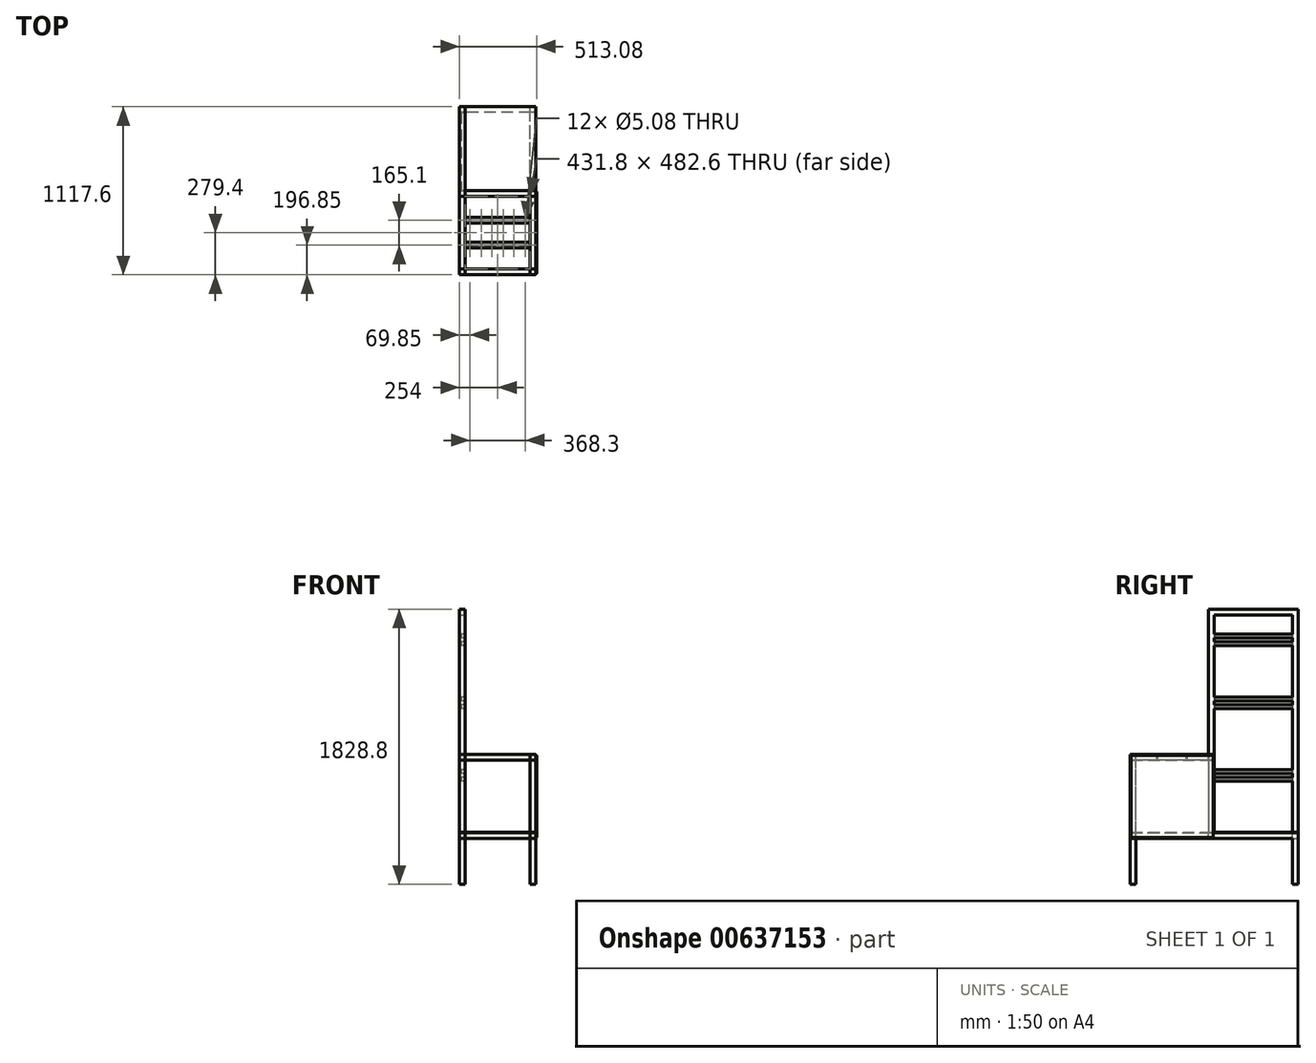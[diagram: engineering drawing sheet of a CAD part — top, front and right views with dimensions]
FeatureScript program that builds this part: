
annotation { "Feature Type Name" : "Feature", "Feature Type Description" : "" }
export const myFeature = defineFeature(function(context is Context, id is Id, definition is map)
    precondition{}
    {
        {
            var Q0;
            Q0=qCreatedBy(makeId("Front.planeOp"),FACE);
            var sketch = newSketch(context, id + "F0", { "sketchPlane" : qUnion([Q0])});
            skLineSegment(sketch, "E0.bottom", {"start": v(-19.05, 19.05) * mm, "end": v(19.05, 19.05) * mm});
            skLineSegment(sketch, "E0.top", {"start": v(-19.05, -19.05) * mm, "end": v(19.05, -19.05) * mm});
            skLineSegment(sketch, "E0.left", {"start": v(-19.05, 19.05) * mm, "end": v(-19.05, -19.05) * mm});
            skLineSegment(sketch, "E0.right", {"start": v(19.05, 19.05) * mm, "end": v(19.05, -19.05) * mm});
            skLineSegment(sketch, "E1", {"start": v(-19.05, 19.05) * mm, "end": v(19.05, -19.05) * mm, "construction": true});
            skLineSegment(sketch, "E2.bottom", {"start": v(450.85, -19.05) * mm, "end": v(488.95, -19.05) * mm});
            skLineSegment(sketch, "E2.top", {"start": v(450.85, 19.05) * mm, "end": v(488.95, 19.05) * mm});
            skLineSegment(sketch, "E2.left", {"start": v(450.85, -19.05) * mm, "end": v(450.85, 19.05) * mm});
            skLineSegment(sketch, "E2.right", {"start": v(488.95, -19.05) * mm, "end": v(488.95, 19.05) * mm});
            skSolve(sketch);
        }
        {
            var Q0;
            Q0 = qSketchRegion(id + "F0", true);
            extrude(context, id + "F1", {"entities" : qUnion([Q0]), "depth" : 1117.6 * mm, "offsetDistance" : 25.4 * mm});
        }
        {
            var Q0;
            Q0=makeQuery(id+"F1.opExtrude","SWEPT_FACE",FACE,{"disambiguationData":[OSD([sQuery(id+"F0.wireOp",EDGE,"E2.bottom")])]});
            var sketch = newSketch(context, id + "F2", { "sketchPlane" : qUnion([Q0])});
            skLineSegment(sketch, "E3.bottom", {"start": v(488.95, 1117.6) * mm, "end": v(450.85, 1117.6) * mm});
            skLineSegment(sketch, "E3.top", {"start": v(488.95, 1079.5) * mm, "end": v(450.85, 1079.5) * mm});
            skLineSegment(sketch, "E3.left", {"start": v(488.95, 1117.6) * mm, "end": v(488.95, 1079.5) * mm});
            skLineSegment(sketch, "E3.right", {"start": v(450.85, 1117.6) * mm, "end": v(450.85, 1079.5) * mm});
            skLineSegment(sketch, "E4.bottom", {"start": v(19.05, 1117.6) * mm, "end": v(-19.05, 1117.6) * mm});
            skLineSegment(sketch, "E4.top", {"start": v(19.05, 1079.5) * mm, "end": v(-19.05, 1079.5) * mm});
            skLineSegment(sketch, "E4.left", {"start": v(19.05, 1117.6) * mm, "end": v(19.05, 1079.5) * mm});
            skLineSegment(sketch, "E4.right", {"start": v(-19.05, 1117.6) * mm, "end": v(-19.05, 1079.5) * mm});
            skSolve(sketch);
        }
        {
            var Q0;
            Q0 = qSketchRegion(id + "F2", true);
            extrude(context, id + "F3", {"entities" : qUnion([Q0]), "depth" : 304.8 * mm, "offsetDistance" : 25.4 * mm, "hasSecondDirection" : true, "secondDirectionOppositeDirection" : true, "secondDirectionDepth" : 558.8 * mm});
        }
        {
            var Q0;
            Q0=makeQuery(id+"F1.opExtrude","SWEPT_FACE",FACE,{"disambiguationData":[OSD([sQuery(id+"F0.wireOp",EDGE,"E0.top")])]});
            var sketch = newSketch(context, id + "F4", { "sketchPlane" : qUnion([Q0])});
            skLineSegment(sketch, "E5.bottom", {"start": v(19.05, 0) * mm, "end": v(-19.05, 0) * mm});
            skLineSegment(sketch, "E5.top", {"start": v(19.05, 38.1) * mm, "end": v(-19.05, 38.1) * mm});
            skLineSegment(sketch, "E5.left", {"start": v(19.05, 0) * mm, "end": v(19.05, 38.1) * mm});
            skLineSegment(sketch, "E5.right", {"start": v(-19.05, 0) * mm, "end": v(-19.05, 38.1) * mm});
            skSolve(sketch);
        }
        {
            var Q0;
            Q0 = qSketchRegion(id + "F4", true);
            extrude(context, id + "F5", {"entities" : qUnion([Q0]), "operationType" : NewBodyOperationType.ADD, "depth" : 304.8 * mm, "offsetDistance" : 25.4 * mm, "hasSecondDirection" : true, "secondDirectionOppositeDirection" : true, "secondDirectionDepth" : 1524 * mm});
        }
        {
            var Q0;
            Q0=makeQuery(id+"F1.opExtrude","SWEPT_FACE",FACE,{"disambiguationData":[OSD([sQuery(id+"F0.wireOp",EDGE,"E0.bottom")])]});
            var sketch = newSketch(context, id + "F6", { "sketchPlane" : qUnion([Q0])});
            skLineSegment(sketch, "E6.bottom", {"start": v(-19.05, -596.9) * mm, "end": v(19.05, -596.9) * mm});
            skLineSegment(sketch, "E6.top", {"start": v(-19.05, -558.8) * mm, "end": v(19.05, -558.8) * mm});
            skLineSegment(sketch, "E6.left", {"start": v(-19.05, -596.9) * mm, "end": v(-19.05, -558.8) * mm});
            skLineSegment(sketch, "E6.right", {"start": v(19.05, -596.9) * mm, "end": v(19.05, -558.8) * mm});
            skSolve(sketch);
        }
        {
            var Q0;
            Q0 = qSketchRegion(id + "F6", true);
            var Q1;
            Q1=makeQuery(id+"F5.opExtrude","CAP_FACE",FACE,{"disambiguationData":[OSD([sQuery(id+"F4.wireOp",EDGE,"E5.bottom"),sQuery(id+"F4.wireOp",EDGE,"E5.top"),sQuery(id+"F4.wireOp",EDGE,"E5.left"),sQuery(id+"F4.wireOp",EDGE,"E5.right")])],"isStart":true});
            extrude(context, id + "F7", {"entities" : qUnion([Q0]), "operationType" : NewBodyOperationType.ADD, "endBound" : BoundingType.UP_TO_SURFACE, "depth" : 25.4 * mm, "endBoundEntityFace" : qUnion([Q1]), "offsetDistance" : 25.4 * mm});
        }
        {
            var Q0;
            Q0=makeQuery(id+"F7.boolean.opBoolean","MERGE",FACE,{"derivedFrom":[makeQuery(id+"F5.boolean.opBoolean","MERGE",FACE,{"derivedFrom":[makeQuery(id+"F1.opExtrude","SWEPT_FACE",FACE,{"disambiguationData":[OSD([sQuery(id+"F0.wireOp",EDGE,"E0.right")])]}),makeQuery(id+"F5.opExtrude","SWEPT_FACE",FACE,{"disambiguationData":[OSD([sQuery(id+"F4.wireOp",EDGE,"E5.left")])]})]}),makeQuery(id+"F7.opExtrude","SWEPT_FACE",FACE,{"disambiguationData":[OSD([sQuery(id+"F6.wireOp",EDGE,"E6.right")])]})]});
            var sketch = newSketch(context, id + "F8", { "sketchPlane" : qUnion([Q0])});
            skLineSegment(sketch, "E7.bottom", {"start": v(-1117.6, 19.05) * mm, "end": v(-1079.5, 19.05) * mm});
            skLineSegment(sketch, "E7.top", {"start": v(-1117.6, -19.05) * mm, "end": v(-1079.5, -19.05) * mm});
            skLineSegment(sketch, "E7.left", {"start": v(-1117.6, 19.05) * mm, "end": v(-1117.6, -19.05) * mm});
            skLineSegment(sketch, "E7.right", {"start": v(-1079.5, 19.05) * mm, "end": v(-1079.5, -19.05) * mm});
            skLineSegment(sketch, "E8.bottom", {"start": v(0, 19.05) * mm, "end": v(-38.1, 19.05) * mm});
            skLineSegment(sketch, "E8.top", {"start": v(0, -19.05) * mm, "end": v(-38.1, -19.05) * mm});
            skLineSegment(sketch, "E8.left", {"start": v(0, 19.05) * mm, "end": v(0, -19.05) * mm});
            skLineSegment(sketch, "E8.right", {"start": v(-38.1, 19.05) * mm, "end": v(-38.1, -19.05) * mm});
            skSolve(sketch);
        }
        {
            var Q0;
            Q0 = qSketchRegion(id + "F8", true);
            var Q1;
            Q1=makeQuery(id+"F1.opExtrude","SWEPT_FACE",FACE,{"disambiguationData":[OSD([sQuery(id+"F0.wireOp",EDGE,"E2.left")])]});
            extrude(context, id + "F9", {"entities" : qUnion([Q0]), "endBound" : BoundingType.UP_TO_SURFACE, "depth" : 25.4 * mm, "endBoundEntityFace" : qUnion([Q1]), "offsetDistance" : 25.4 * mm});
        }
        {
            var Q0;
            Q0=makeQuery(id+"F1.opExtrude","SWEPT_FACE",FACE,{"disambiguationData":[OSD([sQuery(id+"F0.wireOp",EDGE,"E2.bottom")])]});
            var sketch = newSketch(context, id + "F10", { "sketchPlane" : qUnion([Q0])});
            skLineSegment(sketch, "E9.bottom", {"start": v(488.95, 0) * mm, "end": v(450.85, 0) * mm});
            skLineSegment(sketch, "E9.top", {"start": v(488.95, 38.1) * mm, "end": v(450.85, 38.1) * mm});
            skLineSegment(sketch, "E9.left", {"start": v(488.95, 0) * mm, "end": v(488.95, 38.1) * mm});
            skLineSegment(sketch, "E9.right", {"start": v(450.85, 0) * mm, "end": v(450.85, 38.1) * mm});
            skSolve(sketch);
        }
        {
            var Q0;
            Q0 = qSketchRegion(id + "F10", true);
            var Q1;
            Q1=makeQuery(id+"F5.opExtrude","CAP_FACE",FACE,{"disambiguationData":[OSD([sQuery(id+"F4.wireOp",EDGE,"E5.bottom"),sQuery(id+"F4.wireOp",EDGE,"E5.top"),sQuery(id+"F4.wireOp",EDGE,"E5.left"),sQuery(id+"F4.wireOp",EDGE,"E5.right")])],"isStart":false});
            extrude(context, id + "F11", {"entities" : qUnion([Q0]), "operationType" : NewBodyOperationType.ADD, "endBound" : BoundingType.UP_TO_SURFACE, "depth" : 25.4 * mm, "endBoundEntityFace" : qUnion([Q1]), "offsetDistance" : 25.4 * mm});
        }
        {
            var Q0;
            Q0=makeQuery(id+"F1.opExtrude","SWEPT_FACE",FACE,{"disambiguationData":[OSD([sQuery(id+"F0.wireOp",EDGE,"E2.top")])]});
            var sketch = newSketch(context, id + "F12", { "sketchPlane" : qUnion([Q0])});
            skLineSegment(sketch, "E10.bottom", {"start": v(488.95, -596.9) * mm, "end": v(450.85, -596.9) * mm});
            skLineSegment(sketch, "E10.top", {"start": v(488.95, -558.8) * mm, "end": v(450.85, -558.8) * mm});
            skLineSegment(sketch, "E10.left", {"start": v(488.95, -596.9) * mm, "end": v(488.95, -558.8) * mm});
            skLineSegment(sketch, "E10.right", {"start": v(450.85, -596.9) * mm, "end": v(450.85, -558.8) * mm});
            skSolve(sketch);
        }
        {
            var Q0;
            Q0=makeQuery(id+"F12.imprint","IMPRINT",FACE,{"disambiguationData":[TD([[makeQuery(id+"F12.imprint","IMPRINT",EDGE,{"derivedFrom":sQuery(id+"F12.wireOp",EDGE,"E10.bottom")}),-1.0]])]});
            var Q1;
            Q1=makeQuery(id+"F3.opExtrude","CAP_FACE",FACE,{"disambiguationData":[OSD([sQuery(id+"F2.wireOp",EDGE,"E3.bottom"),sQuery(id+"F2.wireOp",EDGE,"E3.top"),sQuery(id+"F2.wireOp",EDGE,"E3.left"),sQuery(id+"F2.wireOp",EDGE,"E3.right")])],"isStart":true});
            extrude(context, id + "F13", {"entities" : qUnion([Q0]), "operationType" : NewBodyOperationType.ADD, "endBound" : BoundingType.UP_TO_SURFACE, "depth" : 25.4 * mm, "endBoundEntityFace" : qUnion([Q1]), "offsetDistance" : 25.4 * mm});
        }
        {
            var Q0;
            Q0=makeQuery(id+"F3.opExtrude","CAP_FACE",FACE,{"disambiguationData":[OSD([sQuery(id+"F2.wireOp",EDGE,"E3.bottom"),sQuery(id+"F2.wireOp",EDGE,"E3.top"),sQuery(id+"F2.wireOp",EDGE,"E3.left"),sQuery(id+"F2.wireOp",EDGE,"E3.right")])],"isStart":true});
            var sketch = newSketch(context, id + "F14", { "sketchPlane" : qUnion([Q0])});
            skLineSegment(sketch, "E11.bottom", {"start": v(-19.05, -558.8) * mm, "end": v(488.95, -558.8) * mm});
            skLineSegment(sketch, "E11.top", {"start": v(-19.05, -1117.6) * mm, "end": v(488.95, -1117.6) * mm});
            skLineSegment(sketch, "E11.left", {"start": v(-19.05, -558.8) * mm, "end": v(-19.05, -1117.6) * mm});
            skLineSegment(sketch, "E11.right", {"start": v(488.95, -558.8) * mm, "end": v(488.95, -1117.6) * mm});
            skLineSegment(sketch, "E12.0", {"start": v(19.05, -596.9) * mm, "end": v(19.05, -1079.5) * mm});
            skLineSegment(sketch, "E12.1", {"start": v(19.05, -596.9) * mm, "end": v(450.85, -596.9) * mm});
            skLineSegment(sketch, "E12.2", {"start": v(450.85, -596.9) * mm, "end": v(450.85, -1079.5) * mm});
            skLineSegment(sketch, "E12.3", {"start": v(19.05, -1079.5) * mm, "end": v(450.85, -1079.5) * mm});
            skSolve(sketch);
        }
        {
            var Q0;
            Q0 = qSketchRegion(id + "F14", true);
            extrude(context, id + "F15", {"entities" : qUnion([Q0]), "oppositeDirection" : true, "depth" : 38.1 * mm, "offsetDistance" : 25.4 * mm});
        }
        {
            var Q0;
            Q0=makeQuery(id+"F7.boolean.opBoolean","MERGE",FACE,{"derivedFrom":[makeQuery(id+"F5.boolean.opBoolean","MERGE",FACE,{"derivedFrom":[makeQuery(id+"F1.opExtrude","SWEPT_FACE",FACE,{"disambiguationData":[OSD([sQuery(id+"F0.wireOp",EDGE,"E0.right")])]}),makeQuery(id+"F5.opExtrude","SWEPT_FACE",FACE,{"disambiguationData":[OSD([sQuery(id+"F4.wireOp",EDGE,"E5.left")])]})]}),makeQuery(id+"F7.opExtrude","SWEPT_FACE",FACE,{"disambiguationData":[OSD([sQuery(id+"F6.wireOp",EDGE,"E6.right")])]})]});
            var sketch = newSketch(context, id + "F16", { "sketchPlane" : qUnion([Q0])});
            skLineSegment(sketch, "E13.bottom", {"start": v(-596.9, 19.05) * mm, "end": v(-558.8, 19.05) * mm});
            skLineSegment(sketch, "E13.top", {"start": v(-596.9, -19.05) * mm, "end": v(-558.8, -19.05) * mm});
            skLineSegment(sketch, "E13.left", {"start": v(-596.9, 19.05) * mm, "end": v(-596.9, -19.05) * mm});
            skLineSegment(sketch, "E13.right", {"start": v(-558.8, 19.05) * mm, "end": v(-558.8, -19.05) * mm});
            skSolve(sketch);
        }
        {
            var Q0;
            Q0 = qSketchRegion(id + "F16", true);
            var Q1;
            Q1=makeQuery(id+"F13.boolean.opBoolean","MERGE",FACE,{"derivedFrom":[makeQuery(id+"F11.boolean.opBoolean","MERGE",FACE,{"derivedFrom":[makeQuery(id+"F1.opExtrude","SWEPT_FACE",FACE,{"disambiguationData":[OSD([sQuery(id+"F0.wireOp",EDGE,"E2.left")])]}),makeQuery(id+"F11.opExtrude","SWEPT_FACE",FACE,{"disambiguationData":[OSD([sQuery(id+"F10.wireOp",EDGE,"E9.right")])]})]}),makeQuery(id+"F13.opExtrude","SWEPT_FACE",FACE,{"disambiguationData":[OSD([sQuery(id+"F12.wireOp",EDGE,"E10.right")])]})]});
            extrude(context, id + "F17", {"entities" : qUnion([Q0]), "endBound" : BoundingType.UP_TO_SURFACE, "depth" : 25.4 * mm, "endBoundEntityFace" : qUnion([Q1]), "offsetDistance" : 25.4 * mm});
        }
        {
            var Q0;
            {var subQ2=sQuery(id+"F4.wireOp",EDGE,"E5.top");Q0=makeQuery(id+"F5.boolean.opBoolean","SPLIT",FACE,{"disambiguationData":[TD([makeQuery(id+"F1.opExtrude","SWEPT_FACE",FACE,{"disambiguationData":[OSD([sQuery(id+"F0.wireOp",EDGE,"E0.bottom")])]})])],"derivedFrom":makeQuery(id+"F5.opExtrude","SWEPT_FACE",FACE,{"disambiguationData":[OSD([subQ2])]})});}
            var sketch = newSketch(context, id + "F18", { "sketchPlane" : qUnion([Q0])});
            skLineSegment(sketch, "E14.bottom", {"start": v(-19.05, 1504.95) * mm, "end": v(19.05, 1504.95) * mm});
            skLineSegment(sketch, "E14.top", {"start": v(-19.05, 1466.85) * mm, "end": v(19.05, 1466.85) * mm});
            skLineSegment(sketch, "E14.left", {"start": v(-19.05, 1504.95) * mm, "end": v(-19.05, 1466.85) * mm});
            skLineSegment(sketch, "E14.right", {"start": v(19.05, 1504.95) * mm, "end": v(19.05, 1466.85) * mm});
            skSolve(sketch);
        }
        {
            var Q0;
            Q0 = qSketchRegion(id + "F18", true);
            var Q1;
            Q1=makeQuery(id+"F7.opExtrude","SWEPT_FACE",FACE,{"disambiguationData":[OSD([sQuery(id+"F6.wireOp",EDGE,"E6.top")])]});
            extrude(context, id + "F19", {"entities" : qUnion([Q0]), "operationType" : NewBodyOperationType.ADD, "endBound" : BoundingType.UP_TO_SURFACE, "depth" : 25.4 * mm, "endBoundEntityFace" : qUnion([Q1]), "offsetDistance" : 25.4 * mm});
        }
        {
            var Q0;
            Q0=makeQuery(id+"F15.opExtrude","SWEPT_FACE",FACE,{"disambiguationData":[OSD([sQuery(id+"F14.wireOp",EDGE,"E12.0")])]});
            var sketch = newSketch(context, id + "F20", { "sketchPlane" : qUnion([Q0])});
            skLineSegment(sketch, "E15.bottom", {"start": v(-736.6, 539.75) * mm, "end": v(-774.7, 539.75) * mm});
            skLineSegment(sketch, "E15.left", {"start": v(-736.6, 539.75) * mm, "end": v(-736.6, 501.65) * mm});
            skLineSegment(sketch, "E16.bottom", {"start": v(-939.8, 539.75) * mm, "end": v(-901.7, 539.75) * mm});
            skLineSegment(sketch, "E16.left", {"start": v(-939.8, 539.75) * mm, "end": v(-939.8, 501.65) * mm});
            skLineSegment(sketch, "E17.0", {"start": v(-933.45, 533.4) * mm, "end": v(-901.7, 533.4) * mm});
            skLineSegment(sketch, "E17.1", {"start": v(-933.45, 533.4) * mm, "end": v(-933.45, 501.65) * mm});
            skLineSegment(sketch, "E18", {"start": v(-939.8, 501.65) * mm, "end": v(-933.45, 501.65) * mm});
            skLineSegment(sketch, "E19", {"start": v(-901.7, 539.75) * mm, "end": v(-901.7, 533.4) * mm});
            skLineSegment(sketch, "E20.0", {"start": v(-742.95, 533.4) * mm, "end": v(-774.7, 533.4) * mm});
            skLineSegment(sketch, "E20.1", {"start": v(-742.95, 533.4) * mm, "end": v(-742.95, 501.65) * mm});
            skLineSegment(sketch, "E21", {"start": v(-742.95, 501.65) * mm, "end": v(-736.6, 501.65) * mm});
            skLineSegment(sketch, "E22", {"start": v(-774.7, 533.4) * mm, "end": v(-774.7, 539.75) * mm});
            skSolve(sketch);
        }
        {
            var Q0;
            Q0 = qSketchRegion(id + "F20", true);
            var Q1;
            Q1=makeQuery(id+"F15.opExtrude","SWEPT_FACE",FACE,{"disambiguationData":[OSD([sQuery(id+"F14.wireOp",EDGE,"E12.2")])]});
            extrude(context, id + "F21", {"entities" : qUnion([Q0]), "endBound" : BoundingType.UP_TO_SURFACE, "depth" : 25.4 * mm, "endBoundEntityFace" : qUnion([Q1]), "offsetDistance" : 25.4 * mm});
        }
        {
            var Q0;
            Q0=makeQuery(id+"F15.opExtrude","SWEPT_FACE",FACE,{"disambiguationData":[OSD([sQuery(id+"F14.wireOp",EDGE,"E12.1")])]});
            var sketch = newSketch(context, id + "F22", { "sketchPlane" : qUnion([Q0])});
            skLineSegment(sketch, "E23.bottom", {"start": v(21.34, 539.75) * mm, "end": v(161.04, 539.75) * mm});
            skLineSegment(sketch, "E23.top", {"start": v(21.34, 679.45) * mm, "end": v(161.04, 679.45) * mm});
            skLineSegment(sketch, "E23.left", {"start": v(21.34, 539.75) * mm, "end": v(21.34, 679.45) * mm});
            skLineSegment(sketch, "E23.right", {"start": v(161.04, 539.75) * mm, "end": v(161.04, 679.45) * mm});
            skLineSegment(sketch, "E24.bottom", {"start": v(166.12, 539.75) * mm, "end": v(305.82, 539.75) * mm});
            skLineSegment(sketch, "E24.top", {"start": v(166.12, 679.45) * mm, "end": v(305.82, 679.45) * mm});
            skLineSegment(sketch, "E24.left", {"start": v(166.12, 539.75) * mm, "end": v(166.12, 679.45) * mm});
            skLineSegment(sketch, "E24.right", {"start": v(305.82, 539.75) * mm, "end": v(305.82, 679.45) * mm});
            skLineSegment(sketch, "E25.bottom", {"start": v(310.9, 539.75) * mm, "end": v(450.6, 539.75) * mm});
            skLineSegment(sketch, "E25.top", {"start": v(310.9, 679.45) * mm, "end": v(450.6, 679.45) * mm});
            skLineSegment(sketch, "E25.left", {"start": v(310.9, 539.75) * mm, "end": v(310.9, 679.45) * mm});
            skLineSegment(sketch, "E25.right", {"start": v(450.6, 539.75) * mm, "end": v(450.6, 679.45) * mm});
            skSolve(sketch);
        }
        {
            var Q0;
            Q0=makeQuery(id+"F19.boolean.opBoolean","MERGE",FACE,{"derivedFrom":[makeQuery(id+"F7.boolean.opBoolean","MERGE",FACE,{"derivedFrom":[makeQuery(id+"F5.boolean.opBoolean","MERGE",FACE,{"derivedFrom":[makeQuery(id+"F1.opExtrude","SWEPT_FACE",FACE,{"disambiguationData":[OSD([sQuery(id+"F0.wireOp",EDGE,"E0.right")])]}),makeQuery(id+"F5.opExtrude","SWEPT_FACE",FACE,{"disambiguationData":[OSD([sQuery(id+"F4.wireOp",EDGE,"E5.left")])]})]}),makeQuery(id+"F7.opExtrude","SWEPT_FACE",FACE,{"disambiguationData":[OSD([sQuery(id+"F6.wireOp",EDGE,"E6.right")])]})]}),makeQuery(id+"F19.opExtrude","SWEPT_FACE",FACE,{"disambiguationData":[OSD([sQuery(id+"F18.wireOp",EDGE,"E14.right")])]})]});
            var sketch = newSketch(context, id + "F23", { "sketchPlane" : qUnion([Q0])});
            skLineSegment(sketch, "E26.bottom", {"start": v(-533.4, 1390.65) * mm, "end": v(-393.7, 1390.65) * mm});
            skLineSegment(sketch, "E26.top", {"start": v(-533.4, 1047.75) * mm, "end": v(-393.7, 1047.75) * mm});
            skLineSegment(sketch, "E26.left", {"start": v(-533.4, 1390.65) * mm, "end": v(-533.4, 1047.75) * mm});
            skLineSegment(sketch, "E26.right", {"start": v(-393.7, 1390.65) * mm, "end": v(-393.7, 1047.75) * mm});
            skLineSegment(sketch, "E27.bottom", {"start": v(-368.3, 1390.65) * mm, "end": v(-228.6, 1390.65) * mm});
            skLineSegment(sketch, "E27.top", {"start": v(-368.3, 1047.75) * mm, "end": v(-228.6, 1047.75) * mm});
            skLineSegment(sketch, "E27.left", {"start": v(-368.3, 1390.65) * mm, "end": v(-368.3, 1047.75) * mm});
            skLineSegment(sketch, "E27.right", {"start": v(-228.6, 1390.65) * mm, "end": v(-228.6, 1047.75) * mm});
            skLineSegment(sketch, "E28.bottom", {"start": v(-203.2, 1390.65) * mm, "end": v(-63.5, 1390.65) * mm});
            skLineSegment(sketch, "E28.top", {"start": v(-203.2, 1047.75) * mm, "end": v(-63.5, 1047.75) * mm});
            skLineSegment(sketch, "E28.left", {"start": v(-203.2, 1390.65) * mm, "end": v(-203.2, 1047.75) * mm});
            skLineSegment(sketch, "E28.right", {"start": v(-63.5, 1390.65) * mm, "end": v(-63.5, 1047.75) * mm});
            skLineSegment(sketch, "E29.bottom", {"start": v(-533.4, 971.55) * mm, "end": v(-393.7, 971.55) * mm});
            skLineSegment(sketch, "E29.top", {"start": v(-533.4, 565.15) * mm, "end": v(-393.7, 565.15) * mm});
            skLineSegment(sketch, "E29.left", {"start": v(-533.4, 971.55) * mm, "end": v(-533.4, 565.15) * mm});
            skLineSegment(sketch, "E29.right", {"start": v(-393.7, 971.55) * mm, "end": v(-393.7, 565.15) * mm});
            skLineSegment(sketch, "E30.bottom", {"start": v(-368.3, 971.55) * mm, "end": v(-228.6, 971.55) * mm});
            skLineSegment(sketch, "E30.top", {"start": v(-368.3, 565.15) * mm, "end": v(-228.6, 565.15) * mm});
            skLineSegment(sketch, "E30.left", {"start": v(-368.3, 971.55) * mm, "end": v(-368.3, 565.15) * mm});
            skLineSegment(sketch, "E30.right", {"start": v(-228.6, 971.55) * mm, "end": v(-228.6, 565.15) * mm});
            skLineSegment(sketch, "E31.bottom", {"start": v(-203.2, 971.55) * mm, "end": v(-63.5, 971.55) * mm});
            skLineSegment(sketch, "E31.top", {"start": v(-203.2, 565.15) * mm, "end": v(-63.5, 565.15) * mm});
            skLineSegment(sketch, "E31.left", {"start": v(-203.2, 971.55) * mm, "end": v(-203.2, 565.15) * mm});
            skLineSegment(sketch, "E31.right", {"start": v(-63.5, 971.55) * mm, "end": v(-63.5, 565.15) * mm});
            skLineSegment(sketch, "E32.bottom", {"start": v(-533.4, 488.95) * mm, "end": v(-393.7, 488.95) * mm});
            skLineSegment(sketch, "E32.top", {"start": v(-533.4, 82.55) * mm, "end": v(-393.7, 82.55) * mm});
            skLineSegment(sketch, "E32.left", {"start": v(-533.4, 488.95) * mm, "end": v(-533.4, 82.55) * mm});
            skLineSegment(sketch, "E32.right", {"start": v(-393.7, 488.95) * mm, "end": v(-393.7, 82.55) * mm});
            skLineSegment(sketch, "E33.bottom", {"start": v(-368.3, 488.95) * mm, "end": v(-228.6, 488.95) * mm});
            skLineSegment(sketch, "E33.top", {"start": v(-368.3, 133.35) * mm, "end": v(-228.6, 133.35) * mm});
            skLineSegment(sketch, "E33.left", {"start": v(-368.3, 488.95) * mm, "end": v(-368.3, 133.35) * mm});
            skLineSegment(sketch, "E33.right", {"start": v(-228.6, 488.95) * mm, "end": v(-228.6, 133.35) * mm});
            skLineSegment(sketch, "E34.bottom", {"start": v(-203.2, 488.95) * mm, "end": v(-63.5, 488.95) * mm});
            skLineSegment(sketch, "E34.top", {"start": v(-203.2, 209.55) * mm, "end": v(-63.5, 209.55) * mm});
            skLineSegment(sketch, "E34.left", {"start": v(-203.2, 488.95) * mm, "end": v(-203.2, 209.55) * mm});
            skLineSegment(sketch, "E34.right", {"start": v(-63.5, 488.95) * mm, "end": v(-63.5, 209.55) * mm});
            skSolve(sketch);
        }
        {
            var Q0;
            Q0=makeQuery(id+"F9.opExtrude","SWEPT_FACE",FACE,{"disambiguationData":[OSD([sQuery(id+"F8.wireOp",EDGE,"E7.bottom")])]});
            var sketch = newSketch(context, id + "F24", { "sketchPlane" : qUnion([Q0])});
            skLineSegment(sketch, "E35.bottom", {"start": v(-19.05, -1117.6) * mm, "end": v(488.95, -1117.6) * mm});
            skLineSegment(sketch, "E35.top", {"start": v(-19.05, 0) * mm, "end": v(488.95, 0) * mm});
            skLineSegment(sketch, "E35.left", {"start": v(-19.05, -1117.6) * mm, "end": v(-19.05, 0) * mm});
            skLineSegment(sketch, "E35.right", {"start": v(488.95, -1117.6) * mm, "end": v(488.95, 0) * mm});
            skSolve(sketch);
        }
        {
            var Q0;
            Q0 = qSketchRegion(id + "F24", true);
            extrude(context, id + "F25", {"entities" : qUnion([Q0]), "depth" : 2.54 * mm, "offsetDistance" : 25.4 * mm});
        }
        {
            var Q0;
            Q0=makeQuery(id+"F15.opExtrude","SWEPT_FACE",FACE,{"disambiguationData":[OSD([sQuery(id+"F14.wireOp",EDGE,"E11.bottom")])]});
            var sketch = newSketch(context, id + "F26", { "sketchPlane" : qUnion([Q0])});
            skLineSegment(sketch, "E36.bottom", {"start": v(-450.85, 501.65) * mm, "end": v(-19.05, 501.65) * mm});
            skLineSegment(sketch, "E36.top", {"start": v(-450.85, 19.05) * mm, "end": v(-19.05, 19.05) * mm});
            skLineSegment(sketch, "E36.left", {"start": v(-450.85, 501.65) * mm, "end": v(-450.85, 19.05) * mm});
            skLineSegment(sketch, "E36.right", {"start": v(-19.05, 501.65) * mm, "end": v(-19.05, 19.05) * mm});
            skSolve(sketch);
        }
        {
            var Q0;
            Q0 = qSketchRegion(id + "F26", true);
            extrude(context, id + "F27", {"entities" : qUnion([Q0]), "oppositeDirection" : true, "depth" : 1.27 * mm, "offsetDistance" : 25.4 * mm});
        }
        {
            var Q0;
            Q0=makeQuery(id+"F3.opExtrude","SWEPT_FACE",FACE,{"disambiguationData":[OSD([sQuery(id+"F2.wireOp",EDGE,"E4.bottom")])]});
            var sketch = newSketch(context, id + "F28", { "sketchPlane" : qUnion([Q0])});
            skLineSegment(sketch, "E37.bottom", {"start": v(19.05, 501.65) * mm, "end": v(450.85, 501.65) * mm});
            skLineSegment(sketch, "E37.top", {"start": v(19.05, 21.6) * mm, "end": v(450.85, 21.6) * mm});
            skLineSegment(sketch, "E37.left", {"start": v(19.05, 501.65) * mm, "end": v(19.05, 21.59) * mm});
            skLineSegment(sketch, "E37.right", {"start": v(450.85, 501.65) * mm, "end": v(450.85, 21.59) * mm});
            skSolve(sketch);
        }
        {
            var Q0;
            Q0 = qSketchRegion(id + "F28", true);
            extrude(context, id + "F29", {"entities" : qUnion([Q0]), "oppositeDirection" : true, "depth" : 1.27 * mm, "offsetDistance" : 25.4 * mm});
        }
        {
            var Q0;
            Q0=makeQuery(id+"F15.opExtrude","SWEPT_FACE",FACE,{"disambiguationData":[OSD([sQuery(id+"F14.wireOp",EDGE,"E11.right")])]});
            var sketch = newSketch(context, id + "F30", { "sketchPlane" : qUnion([Q0])});
            skLineSegment(sketch, "E38.bottom", {"start": v(-565.15, 533.4) * mm, "end": v(-1111.25, 533.4) * mm});
            skLineSegment(sketch, "E38.top", {"start": v(-565.15, -12.7) * mm, "end": v(-1111.25, -12.7) * mm});
            skLineSegment(sketch, "E38.left", {"start": v(-565.15, 533.4) * mm, "end": v(-565.15, -12.7) * mm});
            skLineSegment(sketch, "E38.right", {"start": v(-1111.25, 533.4) * mm, "end": v(-1111.25, -12.7) * mm});
            skSolve(sketch);
        }
        {
            var Q0;
            Q0 = qSketchRegion(id + "F30", true);
            extrude(context, id + "F31", {"entities" : qUnion([Q0]), "depth" : 5.08 * mm, "offsetDistance" : 25.4 * mm});
        }
        {
            var Q0;
            Q0=makeQuery(id+"F7.opExtrude","SWEPT_FACE",FACE,{"disambiguationData":[OSD([sQuery(id+"F6.wireOp",EDGE,"E6.top")])]});
            var sketch = newSketch(context, id + "F32", { "sketchPlane" : qUnion([Q0])});
            skLineSegment(sketch, "E39.bottom", {"start": v(-19.05, 438.15) * mm, "end": v(6.35, 438.15) * mm});
            skLineSegment(sketch, "E39.top", {"start": v(-19.05, 412.75) * mm, "end": v(6.35, 412.75) * mm});
            skLineSegment(sketch, "E39.left", {"start": v(-19.05, 438.15) * mm, "end": v(-19.05, 412.75) * mm});
            skLineSegment(sketch, "E39.right", {"start": v(6.35, 438.15) * mm, "end": v(6.35, 412.75) * mm});
            skLineSegment(sketch, "E40.bottom", {"start": v(-19.05, 920.75) * mm, "end": v(6.35, 920.75) * mm});
            skLineSegment(sketch, "E40.top", {"start": v(-19.05, 895.35) * mm, "end": v(6.35, 895.35) * mm});
            skLineSegment(sketch, "E40.left", {"start": v(-19.05, 920.75) * mm, "end": v(-19.05, 895.35) * mm});
            skLineSegment(sketch, "E40.right", {"start": v(6.35, 920.75) * mm, "end": v(6.35, 895.35) * mm});
            skLineSegment(sketch, "E41.bottom", {"start": v(-19.05, 1339.85) * mm, "end": v(6.35, 1339.85) * mm});
            skLineSegment(sketch, "E41.top", {"start": v(-19.05, 1314.45) * mm, "end": v(6.35, 1314.45) * mm});
            skLineSegment(sketch, "E41.left", {"start": v(-19.05, 1339.85) * mm, "end": v(-19.05, 1314.45) * mm});
            skLineSegment(sketch, "E41.right", {"start": v(6.35, 1339.85) * mm, "end": v(6.35, 1314.45) * mm});
            skLineSegment(sketch, "E42.bottom", {"start": v(-19.05, 1289.05) * mm, "end": v(6.35, 1289.05) * mm});
            skLineSegment(sketch, "E42.top", {"start": v(-19.05, 1263.65) * mm, "end": v(6.35, 1263.65) * mm});
            skLineSegment(sketch, "E42.left", {"start": v(-19.05, 1289.05) * mm, "end": v(-19.05, 1263.65) * mm});
            skLineSegment(sketch, "E42.right", {"start": v(6.35, 1289.05) * mm, "end": v(6.35, 1263.65) * mm});
            skLineSegment(sketch, "E43.bottom", {"start": v(-19.05, 869.95) * mm, "end": v(6.35, 869.95) * mm});
            skLineSegment(sketch, "E43.top", {"start": v(-19.05, 844.55) * mm, "end": v(6.35, 844.55) * mm});
            skLineSegment(sketch, "E43.left", {"start": v(-19.05, 869.95) * mm, "end": v(-19.05, 844.55) * mm});
            skLineSegment(sketch, "E43.right", {"start": v(6.35, 869.95) * mm, "end": v(6.35, 844.55) * mm});
            skLineSegment(sketch, "E44.bottom", {"start": v(-19.05, 387.35) * mm, "end": v(6.35, 387.35) * mm});
            skLineSegment(sketch, "E44.top", {"start": v(-19.05, 361.95) * mm, "end": v(6.35, 361.95) * mm});
            skLineSegment(sketch, "E44.left", {"start": v(-19.05, 387.35) * mm, "end": v(-19.05, 361.95) * mm});
            skLineSegment(sketch, "E44.right", {"start": v(6.35, 387.35) * mm, "end": v(6.35, 361.95) * mm});
            skSolve(sketch);
        }
        {
            var Q0;
            Q0 = qSketchRegion(id + "F32", true);
            var Q1;
            {var subQ2=sQuery(id+"F4.wireOp",EDGE,"E5.top");Q1=makeQuery(id+"F5.boolean.opBoolean","SPLIT",FACE,{"disambiguationData":[TD([makeQuery(id+"F1.opExtrude","SWEPT_FACE",FACE,{"disambiguationData":[OSD([sQuery(id+"F0.wireOp",EDGE,"E0.bottom")])]})])],"derivedFrom":makeQuery(id+"F5.opExtrude","SWEPT_FACE",FACE,{"disambiguationData":[OSD([subQ2])]})});}
            extrude(context, id + "F33", {"entities" : qUnion([Q0]), "operationType" : NewBodyOperationType.ADD, "endBound" : BoundingType.UP_TO_SURFACE, "depth" : 25.4 * mm, "endBoundEntityFace" : qUnion([Q1]), "offsetDistance" : 25.4 * mm});
        }
        {
            var Q0;
            Q0=makeQuery(id+"F21.opExtrude","SWEPT_FACE",FACE,{"disambiguationData":[OSD([sQuery(id+"F20.wireOp",EDGE,"E16.bottom")])]});
            var sketch = newSketch(context, id + "F34", { "sketchPlane" : qUnion([Q0])});
            skLineSegment(sketch, "E45", {"start": v(19.05, -755.65) * mm, "end": v(450.85, -755.65) * mm, "construction": true});
            skLineSegment(sketch, "E46", {"start": v(450.85, -920.75) * mm, "end": v(19.05, -920.75) * mm, "construction": true});
            skCircle(sketch, "E47", {"center": v(50.8, -755.65) * mm, "radius": 2.54 * mm});
            skCircle(sketch, "E48", {"center": v(127, -755.65) * mm, "radius": 2.54 * mm});
            skCircle(sketch, "E49", {"center": v(196.85, -755.65) * mm, "radius": 2.54 * mm});
            skCircle(sketch, "E50", {"center": v(273.05, -755.65) * mm, "radius": 2.54 * mm});
            skCircle(sketch, "E51", {"center": v(342.9, -755.65) * mm, "radius": 2.54 * mm});
            skCircle(sketch, "E52", {"center": v(419.1, -755.65) * mm, "radius": 2.54 * mm});
            skCircle(sketch, "E53", {"center": v(50.8, -920.75) * mm, "radius": 2.54 * mm});
            skCircle(sketch, "E54", {"center": v(127, -920.75) * mm, "radius": 2.54 * mm});
            skCircle(sketch, "E55", {"center": v(196.85, -920.75) * mm, "radius": 2.54 * mm});
            skCircle(sketch, "E56", {"center": v(273.05, -920.75) * mm, "radius": 2.54 * mm});
            skCircle(sketch, "E57", {"center": v(342.9, -920.75) * mm, "radius": 2.54 * mm});
            skCircle(sketch, "E58", {"center": v(419.1, -920.75) * mm, "radius": 2.54 * mm});
            skLineSegment(sketch, "E59", {"start": v(234.95, -755.65) * mm, "end": v(234.95, -920.75) * mm, "construction": true});
            skSolve(sketch);
        }
        {
            var Q0;
            Q0 = qSketchRegion(id + "F34", true);
            var Q1;
            Q1=makeQuery(id+"F21.opExtrude","SWEPT_FACE",FACE,{"disambiguationData":[OSD([sQuery(id+"F20.wireOp",EDGE,"E17.0")])]});
            extrude(context, id + "F35", {"entities" : qUnion([Q0]), "operationType" : NewBodyOperationType.REMOVE, "endBound" : BoundingType.UP_TO_SURFACE, "oppositeDirection" : true, "depth" : 88.9 * mm, "endBoundEntityFace" : qUnion([Q1]), "offsetDistance" : 25.4 * mm});
        }
    });
